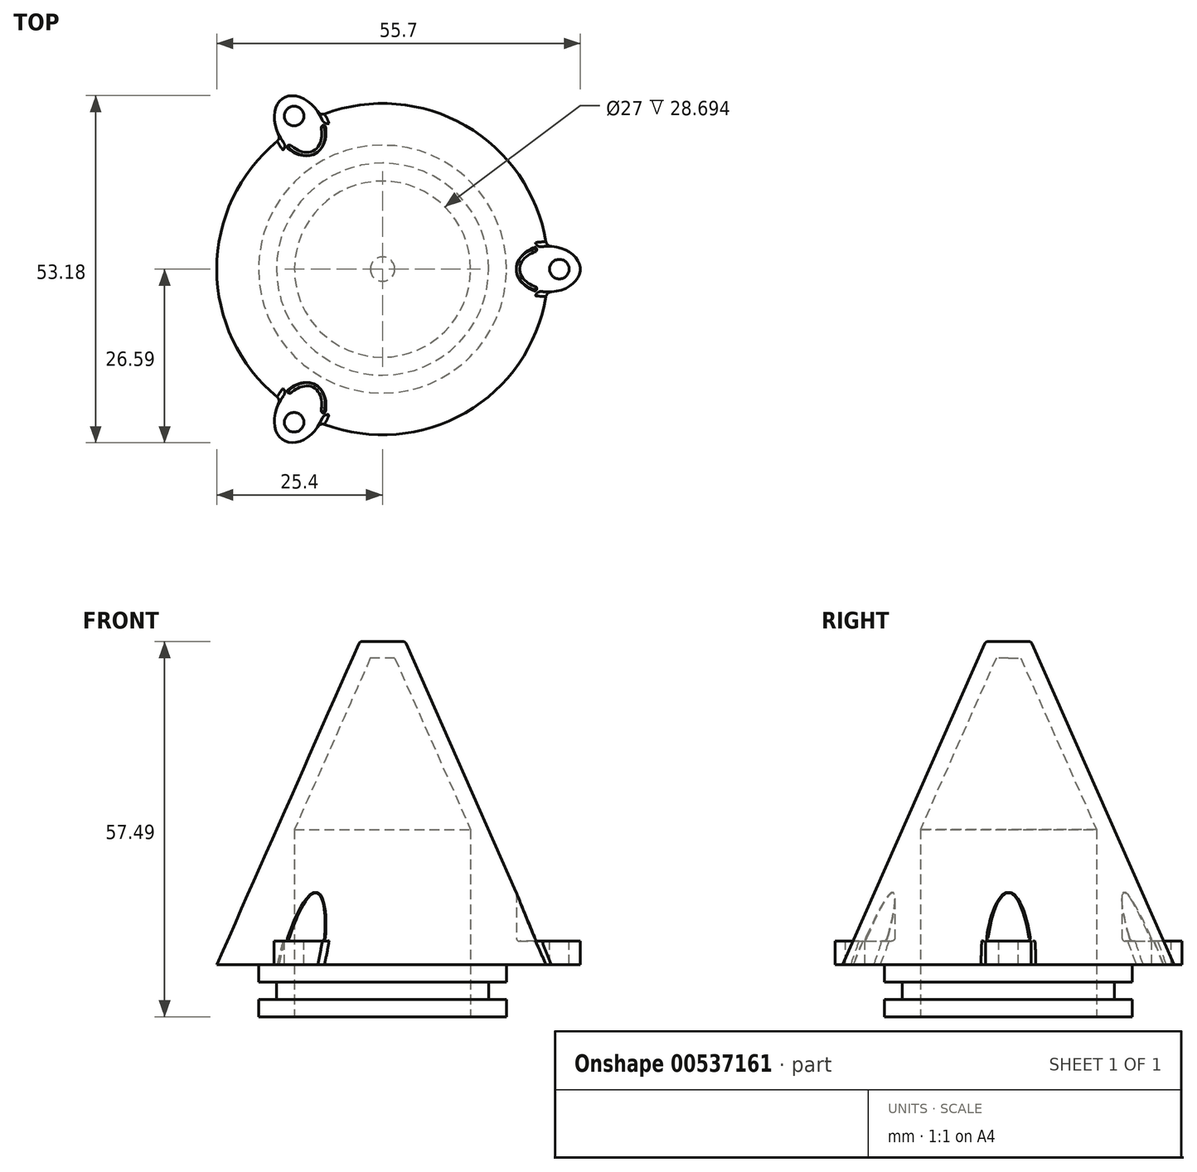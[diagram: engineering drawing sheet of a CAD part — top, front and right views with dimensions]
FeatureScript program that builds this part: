
annotation { "Feature Type Name" : "Feature", "Feature Type Description" : "" }
export const myFeature = defineFeature(function(context is Context, id is Id, definition is map)
    precondition{}
    {
        {
            var Q0;
            Q0=qCreatedBy(makeId("Front.planeOp"),FACE);
            var sketch = newSketch(context, id + "F0", { "sketchPlane" : qUnion([Q0])});
            skLineSegment(sketch, "E0", {"start": v(0, 57.4) * mm, "end": v(0, 0) * mm});
            skLineSegment(sketch, "E1", {"start": v(0, 0) * mm, "end": v(-25.4, 0) * mm});
            skLineSegment(sketch, "E2", {"start": v(-25.4, 0) * mm, "end": v(0, 57.4) * mm});
            skSolve(sketch);
        }
        {
            var Q0;
            Q0=makeQuery(id+"F0.imprint","IMPRINT",FACE,{"disambiguationData":[TD([[makeQuery(id+"F0.imprint","IMPRINT",EDGE,{"derivedFrom":sQuery(id+"F0.wireOp",EDGE,"E0")}),-1.0]])]});
            var Q1;
            Q1=sQuery(id+"F0.wireOp",EDGE,"E0");
            revolve(context, id + "F1", {"entities" : qUnion([Q0]), "axis" : qUnion([Q1]), "revolveType" : RevolveType.FULL});
        }
        {
            var Q0;
            Q0=qCreatedBy(makeId("Front.planeOp"),FACE);
            var sketch = newSketch(context, id + "F2", { "sketchPlane" : qUnion([Q0])});
            skLineSegment(sketch, "E3", {"start": v(-3.5, 49.5) * mm, "end": v(0, 57.4) * mm});
            skLineSegment(sketch, "E4", {"start": v(0, 57.4) * mm, "end": v(3.5, 49.5) * mm});
            skLineSegment(sketch, "E5", {"start": v(-3.5, 49.5) * mm, "end": v(3.5, 49.5) * mm});
            skSolve(sketch);
        }
        {
            var Q0;
            Q0 = qSketchRegion(id + "F2", true);
            extrude(context, id + "F3", {"entities" : qUnion([Q0]), "operationType" : NewBodyOperationType.REMOVE, "depth" : 10 * mm, "offsetDistance" : 25 * mm, "hasSecondDirection" : true, "secondDirectionOppositeDirection" : true, "secondDirectionDepth" : 10 * mm});
        }
        {
            var Q0;
            Q0=makeQuery(id+"F1.opRevolve","SWEPT_FACE",FACE,{"disambiguationData":[OSD([sQuery(id+"F0.wireOp",EDGE,"E1")])]});
            cPlane(context, id + "F4", {"entities" : qUnion([Q0]), "cplaneType" : CPlaneType.OFFSET, "offset" : 3.6 * mm, "oppositeDirection" : true, "width" : 150 * mm, "height" : 150 * mm});
        }
        {
            var Q0;
            Q0=qCreatedBy(id+"F4.planeOp",FACE);
            var sketch = newSketch(context, id + "F5", { "sketchPlane" : qUnion([Q0])});
            skArc(sketch, "E6.0", {"start": v(-9.55, -23.54) * mm, "mid": v(-12.7, -22) * mm, "end": v(-15.6, -20.04) * mm});
            skEllipse(sketch, "E7", {"center": v(25.4, 0) * mm, "majorRadius": 4.9 * mm, "minorRadius": 3.5 * mm, "majorAxis": v(1, 0)});
            skEllipse(sketch, "E8.1.0", {"center": v(-12.7, 22) * mm, "majorRadius": 4.9 * mm, "minorRadius": 3.5 * mm, "majorAxis": v(-0.5, 0.87)});
            skEllipse(sketch, "E8.2.0", {"center": v(-12.7, -22) * mm, "majorRadius": 4.9 * mm, "minorRadius": 3.5 * mm, "majorAxis": v(-0.5, -0.87)});
            skArc(sketch, "E9.trimOffspring", {"start": v(-15.6, 20.04) * mm, "mid": v(-12.7, 22) * mm, "end": v(-9.55, 23.54) * mm});
            skArc(sketch, "E10.trimOffspring", {"start": v(25.16, 3.5) * mm, "mid": v(25.4, 0) * mm, "end": v(25.16, -3.5) * mm});
            skCircle(sketch, "E11", {"center": v(27.1, 0) * mm, "radius": 1.5 * mm});
            skLineSegment(sketch, "E12", {"start": v(28.6, 0) * mm, "end": v(30.3, 0) * mm, "construction": true});
            skCircle(sketch, "E13.1.0", {"center": v(-13.55, 23.47) * mm, "radius": 1.5 * mm});
            skCircle(sketch, "E13.2.0", {"center": v(-13.55, -23.47) * mm, "radius": 1.5 * mm});
            skSolve(sketch);
        }
        {
            var Q0;
            Q0 = qSketchRegion(id + "F5", true);
            var Q1;
            Q1=makeQuery(id+"F3.boolean.opBoolean","COPY",FACE,{"derivedFrom":makeQuery(id+"F3.opExtrude","SWEPT_FACE",FACE,{"disambiguationData":[OSD([sQuery(id+"F2.wireOp",EDGE,"E5")])]})});
            extrude(context, id + "F6", {"entities" : qUnion([Q0]), "operationType" : NewBodyOperationType.REMOVE, "endBound" : BoundingType.UP_TO_SURFACE, "oppositeDirection" : true, "depth" : 25 * mm, "endBoundEntityFace" : qUnion([Q1]), "offsetDistance" : 25 * mm});
        }
        {
            var Q0;
            Q0=makeQuery(id+"F1.opRevolve","SWEPT_FACE",FACE,{"disambiguationData":[OSD([sQuery(id+"F0.wireOp",EDGE,"E1")])]});
            shell(context, id + "F7", {"entities" : qUnion([Q0]), "thickness" : 2.5 * mm});
        }
        {
            var Q0;
            {var subQ0=sQuery(id+"F5.wireOp",EDGE,"E10.trimOffspring");Q0=makeQuery(id+"F5.imprint","IMPRINT",FACE,{"disambiguationData":[TD([[makeQuery(id+"F5.imprint","IMPRINT",EDGE,{"derivedFrom":subQ0}),-1.0]])]});}
            var Q1;
            {var subQ0=sQuery(id+"F5.wireOp",EDGE,"E10.trimOffspring");Q1=makeQuery(id+"F5.imprint","IMPRINT",FACE,{"disambiguationData":[TD([[makeQuery(id+"F5.imprint","IMPRINT",EDGE,{"derivedFrom":subQ0}),1.0]])]});}
            var Q2;
            {var subQ0=sQuery(id+"F5.wireOp",EDGE,"E6.0");Q2=makeQuery(id+"F5.imprint","IMPRINT",FACE,{"disambiguationData":[TD([[makeQuery(id+"F5.imprint","IMPRINT",EDGE,{"derivedFrom":subQ0}),1.0]])]});}
            var Q3;
            {var subQ0=sQuery(id+"F5.wireOp",EDGE,"E6.0");Q3=makeQuery(id+"F5.imprint","IMPRINT",FACE,{"disambiguationData":[TD([[makeQuery(id+"F5.imprint","IMPRINT",EDGE,{"derivedFrom":subQ0}),-1.0]])]});}
            var Q4;
            {var subQ0=sQuery(id+"F5.wireOp",EDGE,"E9.trimOffspring");Q4=makeQuery(id+"F5.imprint","IMPRINT",FACE,{"disambiguationData":[TD([[makeQuery(id+"F5.imprint","IMPRINT",EDGE,{"derivedFrom":subQ0}),-1.0]])]});}
            var Q5;
            {var subQ0=sQuery(id+"F5.wireOp",EDGE,"E9.trimOffspring");Q5=makeQuery(id+"F5.imprint","IMPRINT",FACE,{"disambiguationData":[TD([[makeQuery(id+"F5.imprint","IMPRINT",EDGE,{"derivedFrom":subQ0}),1.0]])]});}
            var Q6;
            Q6=makeQuery(id+"F1.opRevolve","SWEPT_FACE",FACE,{"disambiguationData":[OSD([sQuery(id+"F0.wireOp",EDGE,"E1")])]});
            extrude(context, id + "F8", {"entities" : qUnion([Q0, Q1, Q2, Q3, Q4, Q5]), "operationType" : NewBodyOperationType.ADD, "endBound" : BoundingType.UP_TO_SURFACE, "depth" : 25 * mm, "endBoundEntityFace" : qUnion([Q6]), "offsetDistance" : 25 * mm});
        }
        {
            var Q0;
            {var subQ0=sQuery(id+"F0.wireOp",EDGE,"E1");Q0=makeQuery(id+"F8.boolean.opBoolean","MERGE",FACE,{"derivedFrom":[makeQuery(id+"F1.opRevolve","SWEPT_FACE",FACE,{"disambiguationData":[OSD([subQ0])]}),makeQuery(id+"F8.opExtrude","CAP_FACE",FACE,{"disambiguationData":[OSD([subQ0]),OD(0.0)],"isStart":false}),makeQuery(id+"F8.opExtrude","CAP_FACE",FACE,{"disambiguationData":[OSD([subQ0]),OD(1.0)],"isStart":false}),makeQuery(id+"F8.opExtrude","CAP_FACE",FACE,{"disambiguationData":[OSD([subQ0]),OD(2.0)],"isStart":false})]});}
            var sketch = newSketch(context, id + "F9", { "sketchPlane" : qUnion([Q0])});
            skCircle(sketch, "E14", {"center": v(0, 0) * mm, "radius": 13.5 * mm});
            skSolve(sketch);
        }
        {
            var Q0;
            Q0=makeQuery(id+"F9.imprint","IMPRINT",FACE,{"disambiguationData":[TD([[makeQuery(id+"F9.imprint","IMPRINT",EDGE,{"derivedFrom":sQuery(id+"F9.wireOp",EDGE,"E14")}),-1.0]])]});
            var Q1;
            Q1=makeQuery(id+"F7.opShell","OFFSET_FACE",FACE,{"disambiguationData":[OSD([sQuery(id+"F0.wireOp",EDGE,"E2")])]});
            extrude(context, id + "F10", {"entities" : qUnion([Q0]), "operationType" : NewBodyOperationType.ADD, "endBound" : BoundingType.UP_TO_SURFACE, "oppositeDirection" : true, "depth" : 25 * mm, "endBoundEntityFace" : qUnion([Q1]), "offsetDistance" : 25 * mm});
        }
        {
            var Q0;
            Q0=makeQuery(id+"F3.boolean.opBoolean","INTERSECT",EDGE,{"derivedFrom":[makeQuery(id+"F1.opRevolve","SWEPT_FACE",FACE,{"disambiguationData":[OSD([sQuery(id+"F0.wireOp",EDGE,"E2")])]}),makeQuery(id+"F3.opExtrude","SWEPT_FACE",FACE,{"disambiguationData":[OSD([sQuery(id+"F2.wireOp",EDGE,"E5")])]})]});
            fillet(context, id + "F11", {"entities" : qUnion([Q0]), "radius" : 0.5 * mm, "tangentPropagation" : true, "allowEdgeOverflow" : false});
        }
        {
            var Q0;
            Q0=makeQuery(id+"F6.boolean.opBoolean","COPY",EDGE,{"derivedFrom":makeQuery(id+"F6.opExtrude","CAP_EDGE",EDGE,{"disambiguationData":[OSD([sQuery(id+"F5.wireOp",EDGE,"E8.1.0")])],"isStart":true})});
            var Q1;
            Q1=makeQuery(id+"F6.boolean.opBoolean","COPY",EDGE,{"derivedFrom":makeQuery(id+"F6.opExtrude","CAP_EDGE",EDGE,{"disambiguationData":[OSD([sQuery(id+"F5.wireOp",EDGE,"E7")])],"isStart":true})});
            var Q2;
            Q2=makeQuery(id+"F6.boolean.opBoolean","COPY",EDGE,{"derivedFrom":makeQuery(id+"F6.opExtrude","CAP_EDGE",EDGE,{"disambiguationData":[OSD([sQuery(id+"F5.wireOp",EDGE,"E8.2.0")])],"isStart":true})});
            fillet(context, id + "F12", {"entities" : qUnion([Q0, Q1, Q2]), "radius" : 0.5 * mm, "tangentPropagation" : true, "allowEdgeOverflow" : false});
        }
        {
            var Q0;
            Q0=makeQuery(id+"F12.opFillet","BLEND_EDGE",EDGE,{"disambiguationData":[OD(1.0)],"blendedFrom":[makeQuery(id+"F6.boolean.opBoolean","COPY",EDGE,{"derivedFrom":makeQuery(id+"F6.opExtrude","CAP_EDGE",EDGE,{"disambiguationData":[OSD([sQuery(id+"F5.wireOp",EDGE,"E8.1.0")])],"isStart":true})}),makeQuery(id+"F1.opRevolve","SWEPT_FACE",FACE,{"disambiguationData":[OSD([sQuery(id+"F0.wireOp",EDGE,"E2")])]})],"blendedInto":[makeQuery(id+"F1.opRevolve","SWEPT_FACE",FACE,{"disambiguationData":[OSD([sQuery(id+"F0.wireOp",EDGE,"E2")])]})]});
            var Q1;
            Q1=makeQuery(id+"F6.boolean.opBoolean","INTERSECT",EDGE,{"derivedFrom":[makeQuery(id+"F1.opRevolve","SWEPT_FACE",FACE,{"disambiguationData":[OSD([sQuery(id+"F0.wireOp",EDGE,"E2")])]}),makeQuery(id+"F6.opExtrude","SWEPT_FACE",FACE,{"disambiguationData":[OSD([sQuery(id+"F5.wireOp",EDGE,"E8.1.0")])]})]});
            var Q2;
            Q2=makeQuery(id+"F12.opFillet","BLEND_EDGE",EDGE,{"disambiguationData":[OD(0.0)],"blendedFrom":[makeQuery(id+"F6.boolean.opBoolean","COPY",EDGE,{"derivedFrom":makeQuery(id+"F6.opExtrude","CAP_EDGE",EDGE,{"disambiguationData":[OSD([sQuery(id+"F5.wireOp",EDGE,"E8.1.0")])],"isStart":true})}),makeQuery(id+"F1.opRevolve","SWEPT_FACE",FACE,{"disambiguationData":[OSD([sQuery(id+"F0.wireOp",EDGE,"E2")])]})],"blendedInto":[makeQuery(id+"F1.opRevolve","SWEPT_FACE",FACE,{"disambiguationData":[OSD([sQuery(id+"F0.wireOp",EDGE,"E2")])]})]});
            var Q3;
            Q3=makeQuery(id+"F6.boolean.opBoolean","INTERSECT",EDGE,{"derivedFrom":[makeQuery(id+"F1.opRevolve","SWEPT_FACE",FACE,{"disambiguationData":[OSD([sQuery(id+"F0.wireOp",EDGE,"E2")])]}),makeQuery(id+"F6.opExtrude","SWEPT_FACE",FACE,{"disambiguationData":[OSD([sQuery(id+"F5.wireOp",EDGE,"E7")])]})]});
            var Q4;
            Q4=makeQuery(id+"F12.opFillet","BLEND_EDGE",EDGE,{"disambiguationData":[OD(0.0)],"blendedFrom":[makeQuery(id+"F6.boolean.opBoolean","COPY",EDGE,{"derivedFrom":makeQuery(id+"F6.opExtrude","CAP_EDGE",EDGE,{"disambiguationData":[OSD([sQuery(id+"F5.wireOp",EDGE,"E7")])],"isStart":true})}),makeQuery(id+"F1.opRevolve","SWEPT_FACE",FACE,{"disambiguationData":[OSD([sQuery(id+"F0.wireOp",EDGE,"E2")])]})],"blendedInto":[makeQuery(id+"F1.opRevolve","SWEPT_FACE",FACE,{"disambiguationData":[OSD([sQuery(id+"F0.wireOp",EDGE,"E2")])]})]});
            var Q5;
            Q5=makeQuery(id+"F12.opFillet","BLEND_EDGE",EDGE,{"disambiguationData":[OD(1.0)],"blendedFrom":[makeQuery(id+"F6.boolean.opBoolean","COPY",EDGE,{"derivedFrom":makeQuery(id+"F6.opExtrude","CAP_EDGE",EDGE,{"disambiguationData":[OSD([sQuery(id+"F5.wireOp",EDGE,"E7")])],"isStart":true})}),makeQuery(id+"F1.opRevolve","SWEPT_FACE",FACE,{"disambiguationData":[OSD([sQuery(id+"F0.wireOp",EDGE,"E2")])]})],"blendedInto":[makeQuery(id+"F1.opRevolve","SWEPT_FACE",FACE,{"disambiguationData":[OSD([sQuery(id+"F0.wireOp",EDGE,"E2")])]})]});
            var Q6;
            Q6=makeQuery(id+"F6.boolean.opBoolean","INTERSECT",EDGE,{"derivedFrom":[makeQuery(id+"F1.opRevolve","SWEPT_FACE",FACE,{"disambiguationData":[OSD([sQuery(id+"F0.wireOp",EDGE,"E2")])]}),makeQuery(id+"F6.opExtrude","SWEPT_FACE",FACE,{"disambiguationData":[OSD([sQuery(id+"F5.wireOp",EDGE,"E8.2.0")])]})]});
            var Q7;
            Q7=makeQuery(id+"F12.opFillet","BLEND_EDGE",EDGE,{"disambiguationData":[OD(1.0)],"blendedFrom":[makeQuery(id+"F6.boolean.opBoolean","COPY",EDGE,{"derivedFrom":makeQuery(id+"F6.opExtrude","CAP_EDGE",EDGE,{"disambiguationData":[OSD([sQuery(id+"F5.wireOp",EDGE,"E8.2.0")])],"isStart":true})}),makeQuery(id+"F1.opRevolve","SWEPT_FACE",FACE,{"disambiguationData":[OSD([sQuery(id+"F0.wireOp",EDGE,"E2")])]})],"blendedInto":[makeQuery(id+"F1.opRevolve","SWEPT_FACE",FACE,{"disambiguationData":[OSD([sQuery(id+"F0.wireOp",EDGE,"E2")])]})]});
            var Q8;
            Q8=makeQuery(id+"F12.opFillet","BLEND_EDGE",EDGE,{"disambiguationData":[OD(0.0)],"blendedFrom":[makeQuery(id+"F6.boolean.opBoolean","COPY",EDGE,{"derivedFrom":makeQuery(id+"F6.opExtrude","CAP_EDGE",EDGE,{"disambiguationData":[OSD([sQuery(id+"F5.wireOp",EDGE,"E8.2.0")])],"isStart":true})}),makeQuery(id+"F1.opRevolve","SWEPT_FACE",FACE,{"disambiguationData":[OSD([sQuery(id+"F0.wireOp",EDGE,"E2")])]})],"blendedInto":[makeQuery(id+"F1.opRevolve","SWEPT_FACE",FACE,{"disambiguationData":[OSD([sQuery(id+"F0.wireOp",EDGE,"E2")])]})]});
            fillet(context, id + "F13", {"entities" : qUnion([Q0, Q1, Q2, Q3, Q4, Q5, Q6, Q7, Q8]), "radius" : 0.2 * mm, "tangentPropagation" : true, "allowEdgeOverflow" : false});
        }
        {
            var Q0;
            Q0=makeQuery(id+"F8.boolean.opBoolean","INTERSECT",EDGE,{"disambiguationData":[OD(0.0)],"derivedFrom":[makeQuery(id+"F1.opRevolve","SWEPT_FACE",FACE,{"disambiguationData":[OSD([sQuery(id+"F0.wireOp",EDGE,"E2")])]}),makeQuery(id+"F8.opExtrude","SWEPT_FACE",FACE,{"disambiguationData":[OSD([sQuery(id+"F5.wireOp",EDGE,"E7")])]})]});
            var Q1;
            Q1=makeQuery(id+"F8.boolean.opBoolean","INTERSECT",EDGE,{"disambiguationData":[OD(1.0)],"derivedFrom":[makeQuery(id+"F1.opRevolve","SWEPT_FACE",FACE,{"disambiguationData":[OSD([sQuery(id+"F0.wireOp",EDGE,"E2")])]}),makeQuery(id+"F8.opExtrude","SWEPT_FACE",FACE,{"disambiguationData":[OSD([sQuery(id+"F5.wireOp",EDGE,"E7")])]})]});
            var Q2;
            Q2=makeQuery(id+"F8.boolean.opBoolean","INTERSECT",EDGE,{"disambiguationData":[OD(1.0)],"derivedFrom":[makeQuery(id+"F1.opRevolve","SWEPT_FACE",FACE,{"disambiguationData":[OSD([sQuery(id+"F0.wireOp",EDGE,"E2")])]}),makeQuery(id+"F8.opExtrude","SWEPT_FACE",FACE,{"disambiguationData":[OSD([sQuery(id+"F5.wireOp",EDGE,"E8.2.0")])]})]});
            var Q3;
            Q3=makeQuery(id+"F8.boolean.opBoolean","INTERSECT",EDGE,{"disambiguationData":[OD(0.0)],"derivedFrom":[makeQuery(id+"F1.opRevolve","SWEPT_FACE",FACE,{"disambiguationData":[OSD([sQuery(id+"F0.wireOp",EDGE,"E2")])]}),makeQuery(id+"F8.opExtrude","SWEPT_FACE",FACE,{"disambiguationData":[OSD([sQuery(id+"F5.wireOp",EDGE,"E8.2.0")])]})]});
            var Q4;
            Q4=makeQuery(id+"F8.boolean.opBoolean","INTERSECT",EDGE,{"disambiguationData":[OD(0.0)],"derivedFrom":[makeQuery(id+"F1.opRevolve","SWEPT_FACE",FACE,{"disambiguationData":[OSD([sQuery(id+"F0.wireOp",EDGE,"E2")])]}),makeQuery(id+"F8.opExtrude","SWEPT_FACE",FACE,{"disambiguationData":[OSD([sQuery(id+"F5.wireOp",EDGE,"E8.1.0")])]})]});
            var Q5;
            Q5=makeQuery(id+"F8.boolean.opBoolean","INTERSECT",EDGE,{"disambiguationData":[OD(1.0)],"derivedFrom":[makeQuery(id+"F1.opRevolve","SWEPT_FACE",FACE,{"disambiguationData":[OSD([sQuery(id+"F0.wireOp",EDGE,"E2")])]}),makeQuery(id+"F8.opExtrude","SWEPT_FACE",FACE,{"disambiguationData":[OSD([sQuery(id+"F5.wireOp",EDGE,"E8.1.0")])]})]});
            fillet(context, id + "F14", {"entities" : qUnion([Q0, Q1, Q2, Q3, Q4, Q5]), "radius" : 0.8 * mm, "tangentPropagation" : true, "allowEdgeOverflow" : false});
        }
        {
            var Q0;
            {var subQ0=sQuery(id+"F5.wireOp",EDGE,"E8.2.0");Q0=makeQuery(id+"F12.opFillet","TWEAK_EDGE",EDGE,{"derivedFrom":[makeQuery(id+"F6.boolean.opBoolean","INTERSECT",VERTEX,{"disambiguationData":[OD(1.0)],"derivedFrom":[makeQuery(id+"F1.opRevolve","SWEPT_FACE",FACE,{"disambiguationData":[OSD([sQuery(id+"F0.wireOp",EDGE,"E2")])]}),makeQuery(id+"F6.opExtrude","SWEPT_FACE",FACE,{"disambiguationData":[OSD([subQ0])]}),makeQuery(id+"F6.opExtrude","CAP_FACE",FACE,{"disambiguationData":[OSD([subQ0])],"isStart":true})]})]});}
            var Q1;
            {var subQ0=sQuery(id+"F5.wireOp",EDGE,"E8.2.0");Q1=makeQuery(id+"F12.opFillet","TWEAK_EDGE",EDGE,{"derivedFrom":[makeQuery(id+"F6.boolean.opBoolean","INTERSECT",VERTEX,{"disambiguationData":[OD(0.0)],"derivedFrom":[makeQuery(id+"F1.opRevolve","SWEPT_FACE",FACE,{"disambiguationData":[OSD([sQuery(id+"F0.wireOp",EDGE,"E2")])]}),makeQuery(id+"F6.opExtrude","SWEPT_FACE",FACE,{"disambiguationData":[OSD([subQ0])]}),makeQuery(id+"F6.opExtrude","CAP_FACE",FACE,{"disambiguationData":[OSD([subQ0])],"isStart":true})]})]});}
            var Q2;
            {var subQ0=sQuery(id+"F5.wireOp",EDGE,"E8.1.0");Q2=makeQuery(id+"F12.opFillet","TWEAK_EDGE",EDGE,{"derivedFrom":[makeQuery(id+"F6.boolean.opBoolean","INTERSECT",VERTEX,{"disambiguationData":[OD(0.0)],"derivedFrom":[makeQuery(id+"F1.opRevolve","SWEPT_FACE",FACE,{"disambiguationData":[OSD([sQuery(id+"F0.wireOp",EDGE,"E2")])]}),makeQuery(id+"F6.opExtrude","SWEPT_FACE",FACE,{"disambiguationData":[OSD([subQ0])]}),makeQuery(id+"F6.opExtrude","CAP_FACE",FACE,{"disambiguationData":[OSD([subQ0])],"isStart":true})]})]});}
            var Q3;
            {var subQ0=sQuery(id+"F5.wireOp",EDGE,"E8.1.0");Q3=makeQuery(id+"F12.opFillet","TWEAK_EDGE",EDGE,{"derivedFrom":[makeQuery(id+"F6.boolean.opBoolean","INTERSECT",VERTEX,{"disambiguationData":[OD(1.0)],"derivedFrom":[makeQuery(id+"F1.opRevolve","SWEPT_FACE",FACE,{"disambiguationData":[OSD([sQuery(id+"F0.wireOp",EDGE,"E2")])]}),makeQuery(id+"F6.opExtrude","SWEPT_FACE",FACE,{"disambiguationData":[OSD([subQ0])]}),makeQuery(id+"F6.opExtrude","CAP_FACE",FACE,{"disambiguationData":[OSD([subQ0])],"isStart":true})]})]});}
            var Q4;
            {var subQ0=sQuery(id+"F5.wireOp",EDGE,"E7");Q4=makeQuery(id+"F12.opFillet","TWEAK_EDGE",EDGE,{"derivedFrom":[makeQuery(id+"F6.boolean.opBoolean","INTERSECT",VERTEX,{"disambiguationData":[OD(0.0)],"derivedFrom":[makeQuery(id+"F1.opRevolve","SWEPT_FACE",FACE,{"disambiguationData":[OSD([sQuery(id+"F0.wireOp",EDGE,"E2")])]}),makeQuery(id+"F6.opExtrude","SWEPT_FACE",FACE,{"disambiguationData":[OSD([subQ0])]}),makeQuery(id+"F6.opExtrude","CAP_FACE",FACE,{"disambiguationData":[OSD([subQ0])],"isStart":true})]})]});}
            var Q5;
            {var subQ0=sQuery(id+"F5.wireOp",EDGE,"E7");Q5=makeQuery(id+"F12.opFillet","TWEAK_EDGE",EDGE,{"derivedFrom":[makeQuery(id+"F6.boolean.opBoolean","INTERSECT",VERTEX,{"disambiguationData":[OD(1.0)],"derivedFrom":[makeQuery(id+"F1.opRevolve","SWEPT_FACE",FACE,{"disambiguationData":[OSD([sQuery(id+"F0.wireOp",EDGE,"E2")])]}),makeQuery(id+"F6.opExtrude","SWEPT_FACE",FACE,{"disambiguationData":[OSD([subQ0])]}),makeQuery(id+"F6.opExtrude","CAP_FACE",FACE,{"disambiguationData":[OSD([subQ0])],"isStart":true})]})]});}
            fillet(context, id + "F15", {"entities" : qUnion([Q0, Q1, Q2, Q3, Q4, Q5]), "radius" : 0.1 * mm, "tangentPropagation" : true, "allowEdgeOverflow" : false});
        }
        {
            var Q0;
            {var subQ0=sQuery(id+"F0.wireOp",EDGE,"E1");Q0=makeQuery(id+"F10.boolean.opBoolean","MERGE",FACE,{"derivedFrom":[makeQuery(id+"F8.boolean.opBoolean","MERGE",FACE,{"derivedFrom":[makeQuery(id+"F1.opRevolve","SWEPT_FACE",FACE,{"disambiguationData":[OSD([subQ0])]}),makeQuery(id+"F8.opExtrude","CAP_FACE",FACE,{"disambiguationData":[OSD([subQ0]),OD(0.0)],"isStart":false}),makeQuery(id+"F8.opExtrude","CAP_FACE",FACE,{"disambiguationData":[OSD([subQ0]),OD(1.0)],"isStart":false}),makeQuery(id+"F8.opExtrude","CAP_FACE",FACE,{"disambiguationData":[OSD([subQ0]),OD(2.0)],"isStart":false})]}),makeQuery(id+"F10.opExtrude","CAP_FACE",FACE,{"disambiguationData":[OSD([subQ0,sQuery(id+"F0.wireOp",EDGE,"E2"),sQuery(id+"F5.wireOp",EDGE,"E7"),sQuery(id+"F5.wireOp",EDGE,"E8.1.0"),sQuery(id+"F5.wireOp",EDGE,"E8.2.0"),sQuery(id+"F9.wireOp",EDGE,"E14")])],"isStart":true})]});}
            var sketch = newSketch(context, id + "F16", { "sketchPlane" : qUnion([Q0])});
            skCircle(sketch, "E15.0", {"center": v(0, 0) * mm, "radius": 13.5 * mm});
            skCircle(sketch, "E16.0", {"center": v(0, 0) * mm, "radius": 16.25 * mm});
            skCircle(sketch, "E17.0", {"center": v(0, 0) * mm, "radius": 19 * mm});
            skSolve(sketch);
        }
        {
            var Q0;
            Q0=makeQuery(id+"F16.imprint","IMPRINT",FACE,{"disambiguationData":[TD([[makeQuery(id+"F16.imprint","IMPRINT",EDGE,{"derivedFrom":sQuery(id+"F16.wireOp",EDGE,"E15.0")}),-1.0]])]});
            var Q1;
            Q1=makeQuery(id+"F16.imprint","IMPRINT",FACE,{"disambiguationData":[TD([[makeQuery(id+"F16.imprint","IMPRINT",EDGE,{"derivedFrom":sQuery(id+"F16.wireOp",EDGE,"E16.0")}),-1.0]])]});
            extrude(context, id + "F17", {"entities" : qUnion([Q0, Q1]), "operationType" : NewBodyOperationType.ADD, "depth" : 2.66 * mm, "offsetDistance" : 25 * mm});
        }
        {
            var Q0;
            Q0=makeQuery(id+"F17.opExtrude","CAP_FACE",FACE,{"disambiguationData":[OSD([sQuery(id+"F16.wireOp",EDGE,"E15.0"),sQuery(id+"F16.wireOp",EDGE,"E17.0")])],"isStart":false});
            var sketch = newSketch(context, id + "F18", { "sketchPlane" : qUnion([Q0])});
            skCircle(sketch, "E18.0", {"center": v(0, 0) * mm, "radius": 16.25 * mm});
            skSolve(sketch);
        }
        {
            var Q0;
            Q0=makeQuery(id+"F18.imprint","IMPRINT",FACE,{"disambiguationData":[TD([[makeQuery(id+"F18.imprint","IMPRINT",EDGE,{"derivedFrom":sQuery(id+"F18.wireOp",EDGE,"E18.0")}),1.0]])]});
            extrude(context, id + "F19", {"entities" : qUnion([Q0]), "operationType" : NewBodyOperationType.ADD, "depth" : 2.66 * mm, "offsetDistance" : 25 * mm});
        }
        {
            var Q0;
            Q0=makeQuery(id+"F19.opExtrude","CAP_FACE",FACE,{"disambiguationData":[OSD([sQuery(id+"F16.wireOp",EDGE,"E15.0"),sQuery(id+"F18.wireOp",EDGE,"E18.0")])],"isStart":false});
            var sketch = newSketch(context, id + "F20", { "sketchPlane" : qUnion([Q0])});
            skCircle(sketch, "E19.0", {"center": v(0, 0) * mm, "radius": 19 * mm});
            skCircle(sketch, "E20.0", {"center": v(0, 0) * mm, "radius": 13.5 * mm});
            skSolve(sketch);
        }
        {
            var Q0;
            Q0 = qSketchRegion(id + "F20", true);
            extrude(context, id + "F21", {"entities" : qUnion([Q0]), "operationType" : NewBodyOperationType.ADD, "depth" : 2.66 * mm, "offsetDistance" : 25 * mm});
        }
    });
